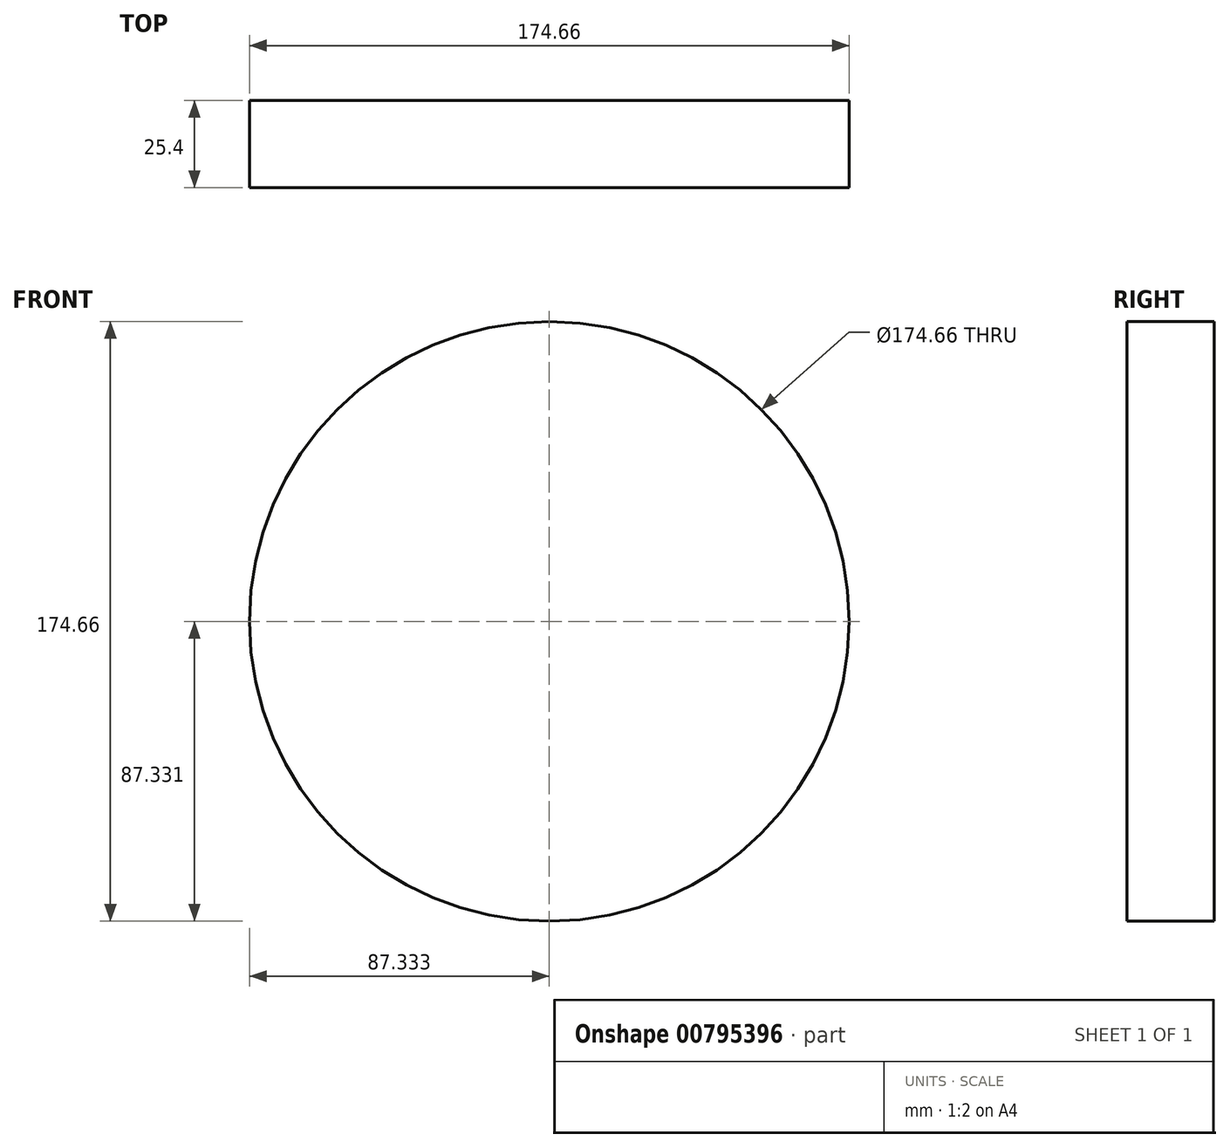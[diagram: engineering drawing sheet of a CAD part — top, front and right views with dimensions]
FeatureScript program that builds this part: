
annotation { "Feature Type Name" : "Feature", "Feature Type Description" : "" }
export const myFeature = defineFeature(function(context is Context, id is Id, definition is map)
    precondition{}
    {
        {
            var Q0;
            Q0=qCreatedBy(makeId("Front.planeOp"),FACE);
            var sketch = newSketch(context, id + "F0", { "sketchPlane" : qUnion([Q0])});
            skCircle(sketch, "E0", {"center": v(11.14, 35.56) * mm, "radius": 87.33 * mm});
            skCircle(sketch, "E1", {"center": v(32.7, 44.5) * mm, "radius": 40.68 * mm});
            skSolve(sketch);
        }
        {
            var Q0;
            Q0=sQuery(id+"F0.wireOp",EDGE,"E0");
            extrude(context, id + "F1", {"bodyType" : ToolBodyType.SURFACE, "surfaceEntities" : qUnion([Q0]), "oppositeDirection" : true, "depth" : 25.4 * mm, "offsetDistance" : 25.4 * mm});
        }
    });
